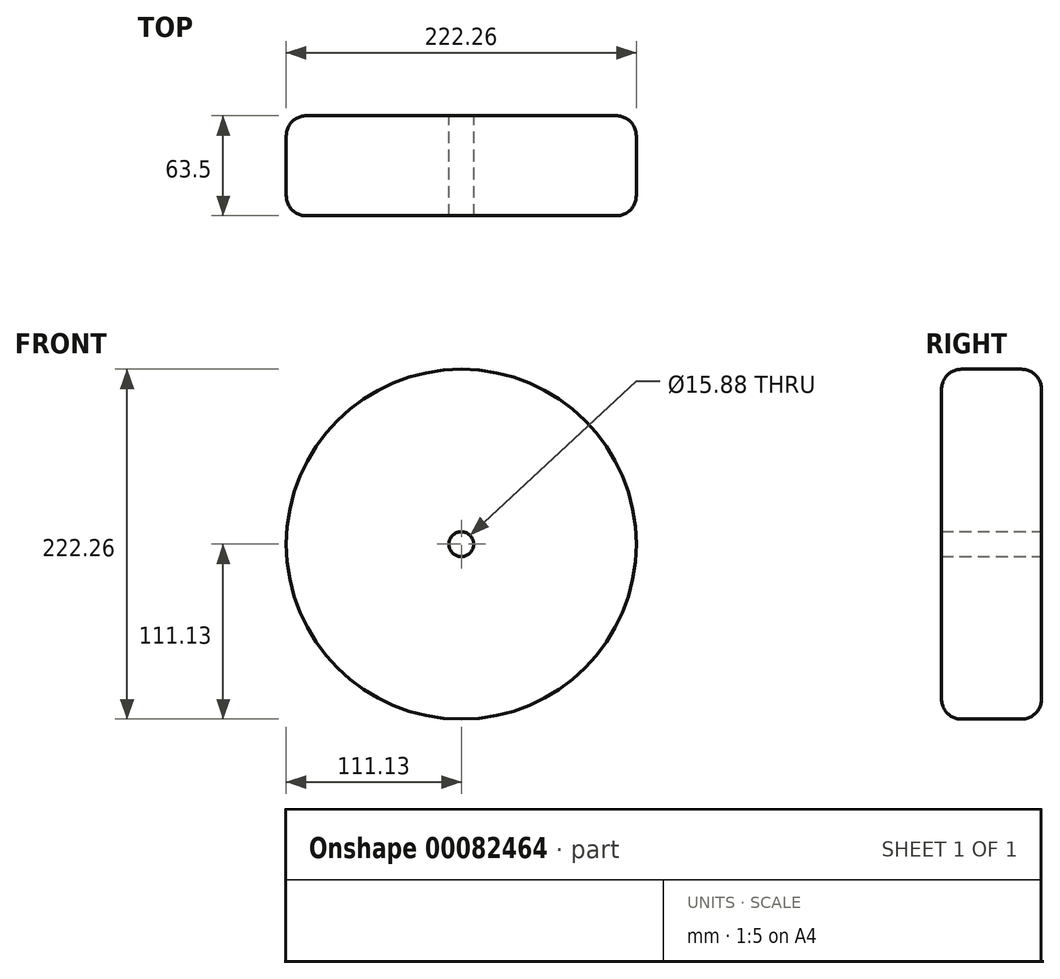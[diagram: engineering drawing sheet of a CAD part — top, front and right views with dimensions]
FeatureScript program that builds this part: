
annotation { "Feature Type Name" : "Feature", "Feature Type Description" : "" }
export const myFeature = defineFeature(function(context is Context, id is Id, definition is map)
    precondition{}
    {
        {
            var Q0;
            Q0=qCreatedBy(makeId("Front.planeOp"),FACE);
            var sketch = newSketch(context, id + "F0", { "sketchPlane" : qUnion([Q0])});
            skCircle(sketch, "E0", {"center": v(0, 0) * mm, "radius": 111.13 * mm});
            skCircle(sketch, "E1", {"center": v(0, 0) * mm, "radius": 7.94 * mm});
            skSolve(sketch);
        }
        {
            var Q0;
            Q0=makeQuery(id+"F0.imprint","IMPRINT",FACE,{"disambiguationData":[TD([[makeQuery(id+"F0.imprint","IMPRINT",EDGE,{"derivedFrom":sQuery(id+"F0.wireOp",EDGE,"E0")}),1.0]])]});
            extrude(context, id + "F1", {"entities" : qUnion([Q0]), "depth" : 63.5 * mm});
        }
        {
            var Q0;
            Q0=makeQuery(id+"F1.opExtrude","CAP_EDGE",EDGE,{"disambiguationData":[OSD([sQuery(id+"F0.wireOp",EDGE,"E0")])],"isStart":false});
            fillet(context, id + "F2", {"entities" : qUnion([Q0]), "radius" : 12.7 * mm, "tangentPropagation" : true, "allowEdgeOverflow" : false});
        }
        {
            var Q0;
            Q0=makeQuery(id+"F1.opExtrude","CAP_EDGE",EDGE,{"disambiguationData":[OSD([sQuery(id+"F0.wireOp",EDGE,"E0")])],"isStart":true});
            fillet(context, id + "F3", {"entities" : qUnion([Q0]), "radius" : 12.7 * mm, "tangentPropagation" : true, "allowEdgeOverflow" : false});
        }
    });
